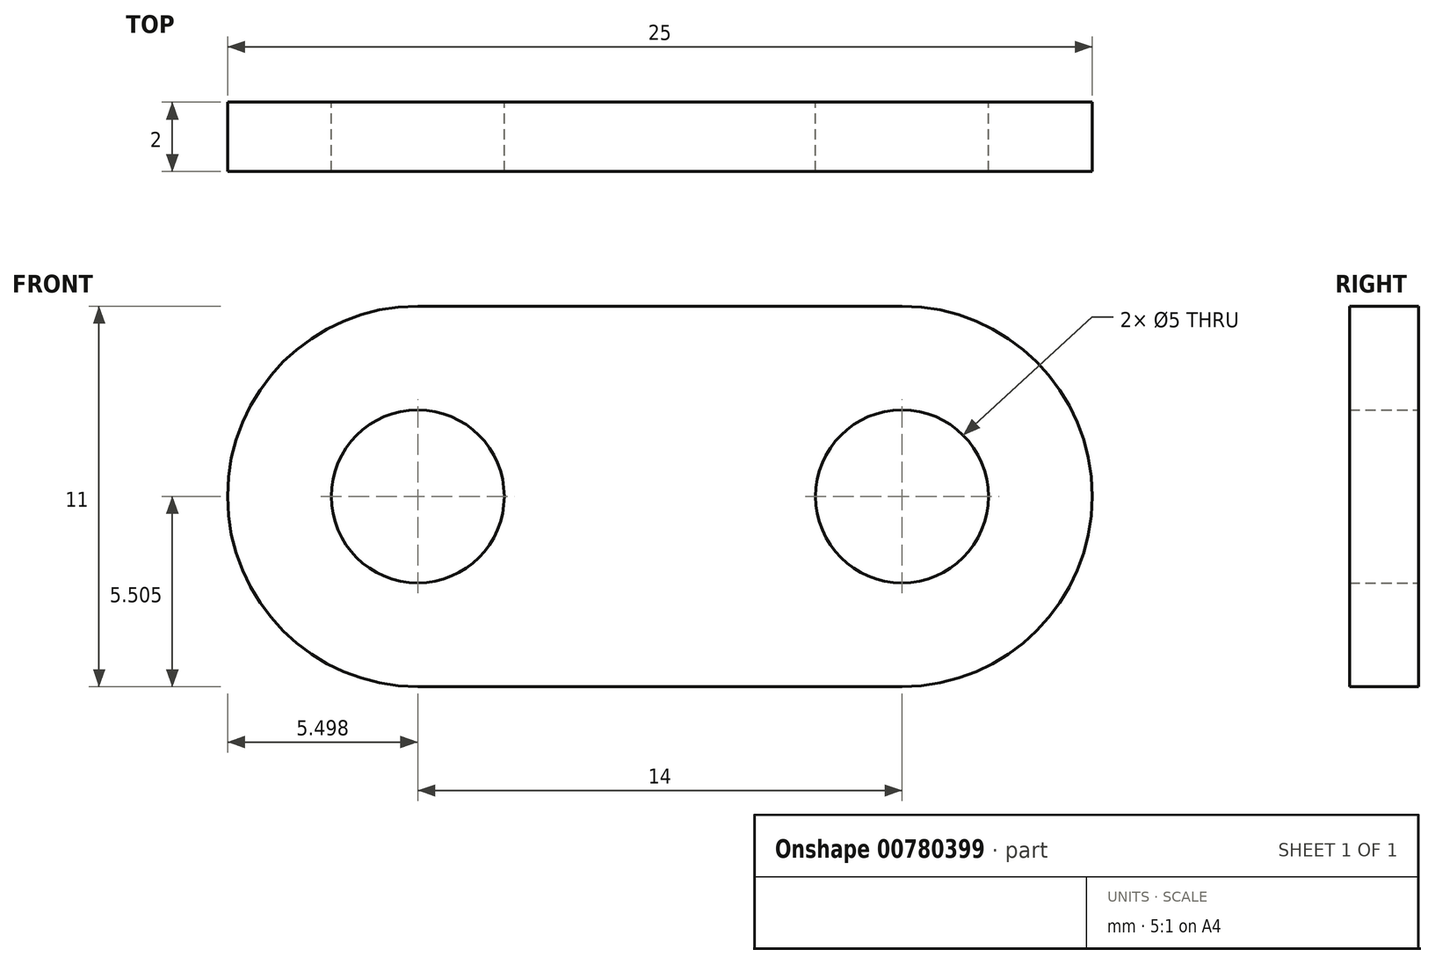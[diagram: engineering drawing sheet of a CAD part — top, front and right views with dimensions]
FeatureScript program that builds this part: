
annotation { "Feature Type Name" : "Feature", "Feature Type Description" : "" }
export const myFeature = defineFeature(function(context is Context, id is Id, definition is map)
    precondition{}
    {
        {
            var Q0;
            Q0=qCreatedBy(makeId("Front.planeOp"),FACE);
            var sketch = newSketch(context, id + "F0", { "sketchPlane" : qUnion([Q0])});
            skLineSegment(sketch, "E0", {"start": v(-8.08, 6.87) * mm, "end": v(5.92, 6.87) * mm});
            skLineSegment(sketch, "E1", {"start": v(-8.08, -4.13) * mm, "end": v(5.92, -4.13) * mm});
            skArc(sketch, "E2", {"start": v(-8.08, 6.87) * mm, "mid": v(-13.58, 1.37) * mm, "end": v(-8.08, -4.13) * mm});
            skArc(sketch, "E3", {"start": v(5.92, -4.13) * mm, "mid": v(11.42, 1.37) * mm, "end": v(5.92, 6.87) * mm});
            skCircle(sketch, "E4", {"center": v(-8.08, 1.37) * mm, "radius": 2.5 * mm});
            skCircle(sketch, "E5", {"center": v(5.92, 1.37) * mm, "radius": 2.5 * mm});
            skSolve(sketch);
        }
        {
            var Q0;
            Q0 = qSketchRegion(id + "F0", true);
            extrude(context, id + "F1", {"entities" : qUnion([Q0]), "depth" : 2 * mm, "offsetDistance" : 25.4 * mm});
        }
    });
